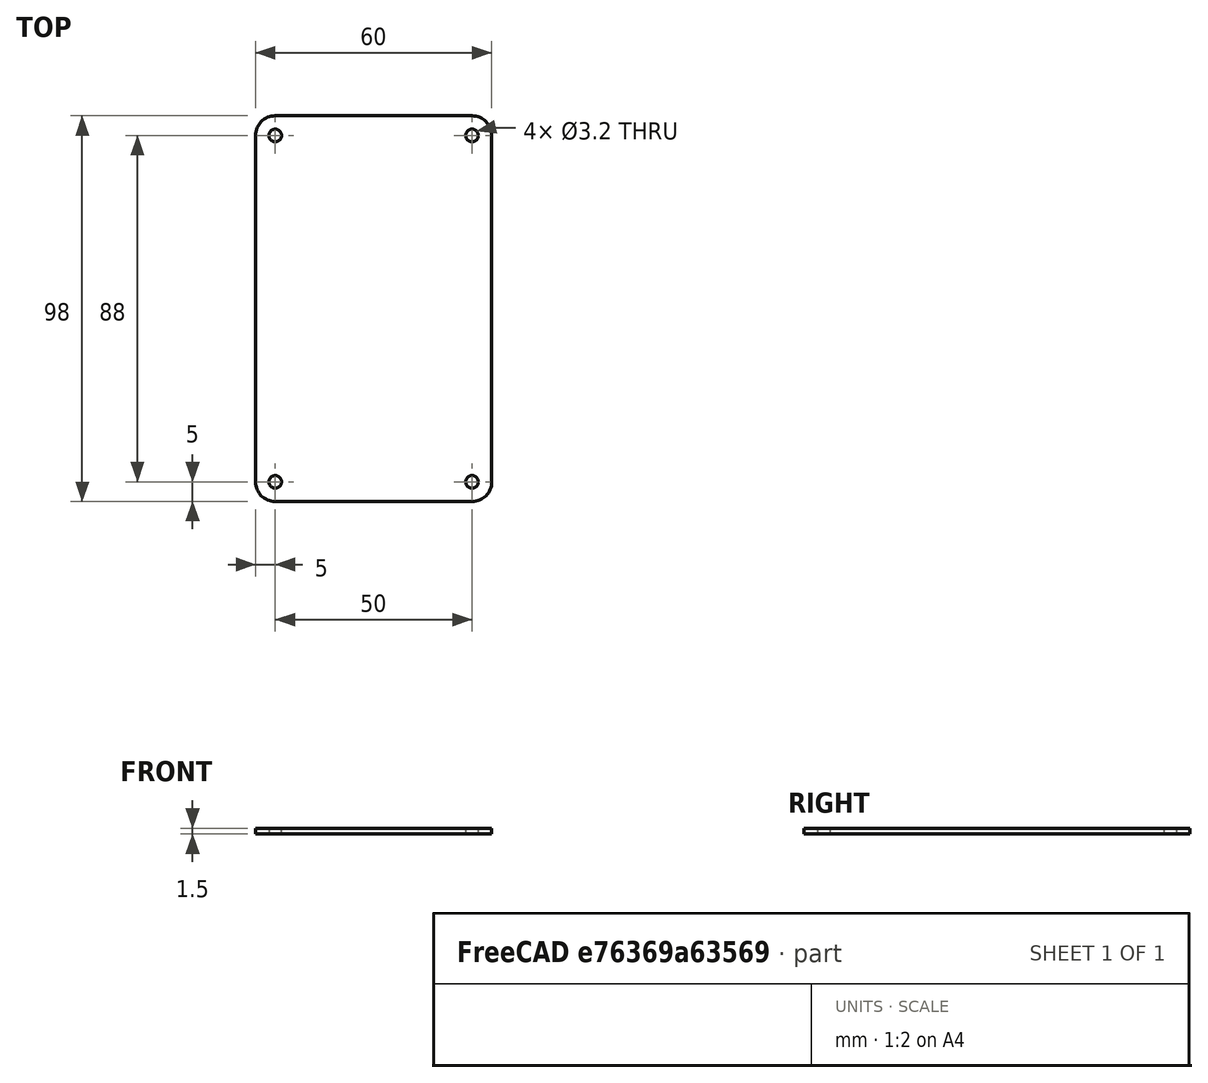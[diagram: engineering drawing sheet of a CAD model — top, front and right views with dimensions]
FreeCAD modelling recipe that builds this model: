
FCSTD DOCUMENT  (FreeCAD 0.17R12802 (Git))
Label: Keep_OUT
License: All rights reserved
LicenseURL: http://en.wikipedia.org/wiki/All_rights_reserved
objects: Sketcher::SketchObject×2, Part::FeaturePython×1, App::DocumentObjectGroupPython×1
note: 3 computed .brp shape members not serialized (recipe doc carries the construction recipe); baked Part::Feature solids carry a one-line shape summary decoded from their .brp

FEATURE [Sketcher::SketchObject] Sketch
  sketch-geometry (8):
    g0: LineSegment StartX=25 StartY=49 StartZ=0 EndX=-25 EndY=49 EndZ=0
    g1: LineSegment StartX=-30 StartY=44 StartZ=0 EndX=-30 EndY=-44 EndZ=0
    g2: LineSegment StartX=-25 StartY=-49 StartZ=0 EndX=25 EndY=-49 EndZ=0
    g3: LineSegment StartX=30 StartY=-44 StartZ=0 EndX=30 EndY=44 EndZ=0
    g4: ArcOfCircle CenterX=-25 CenterY=44 CenterZ=0 NormalX=0 NormalY=0 NormalZ=1 AngleXU=0 Radius=5 StartAngle=1.5708 EndAngle=3.14159
    g5: ArcOfCircle CenterX=-25 CenterY=-44 CenterZ=0 NormalX=0 NormalY=0 NormalZ=1 AngleXU=0 Radius=5 StartAngle=3.14159 EndAngle=4.71239
    g6: ArcOfCircle CenterX=25 CenterY=-44 CenterZ=0 NormalX=0 NormalY=0 NormalZ=1 AngleXU=0 Radius=5 StartAngle=4.71239 EndAngle=6.28319
    g7: ArcOfCircle CenterX=25 CenterY=44 CenterZ=0 NormalX=0 NormalY=0 NormalZ=1 AngleXU=0 Radius=5 StartAngle=0 EndAngle=1.5708
  constraints (20):
    c: Horizontal(g0)
    c: Tangent(g0,g4) = -1.5708
    c: Tangent(g1,g4) = -1.5708
    c: Tangent(g1,g5) = -1.5708
    c: Tangent(g2,g5) = -1.5708
    c: Tangent(g3,g6) = -1.5708
    c: Tangent(g2,g6) = -1.5708
    c: Tangent(g0,g7) = -1.5708
    c: Tangent(g3,g7) = -1.5708
    c: Vertical(g3)
    c: Vertical(g1)
    c: Horizontal(g2)
    c: Radius(g4) = 5
    c: Radius(g7) = 5
    c: DistanceX(g1,g3) = 60
    c: Radius(g5) = 5
    c: Radius(g6) = 5
    c: DistanceY(g2,g0) = 98
    c: DistanceY(g2,g-1) = 49
    c: DistanceX(g-1,g3) = 30
FEATURE [Sketcher::SketchObject] Sketch001
  sketch-geometry (8):
    g0: Circle CenterX=-25 CenterY=44 CenterZ=0 NormalX=0 NormalY=0 NormalZ=1 AngleXU=0 Radius=1.6
    g1: Circle CenterX=25 CenterY=44 CenterZ=0 NormalX=0 NormalY=0 NormalZ=1 AngleXU=0 Radius=1.6
    g2: LineSegment [constr] StartX=-25 StartY=-44 StartZ=0 EndX=25 EndY=-44 EndZ=0
    g3: LineSegment [constr] StartX=25 StartY=-44 StartZ=0 EndX=25 EndY=44 EndZ=0
    g4: LineSegment [constr] StartX=25 StartY=44 StartZ=0 EndX=-25 EndY=44 EndZ=0
    g5: LineSegment [constr] StartX=-25 StartY=44 StartZ=0 EndX=-25 EndY=-44 EndZ=0
    g6: Circle CenterX=-25 CenterY=-44 CenterZ=0 NormalX=0 NormalY=0 NormalZ=1 AngleXU=0 Radius=1.6
    g7: Circle CenterX=25 CenterY=-44 CenterZ=0 NormalX=0 NormalY=0 NormalZ=1 AngleXU=0 Radius=1.6
  constraints (20):
    c: Radius(g0) = 1.6
    c: DistanceX(g0,g-1) = 25
    c: DistanceY(g-1,g0) = 44
    c: Radius(g1) = 1.6
    c: Coincident(g2,g3)
    c: Coincident(g3,g4)
    c: Coincident(g4,g5)
    c: Coincident(g5,g2)
    c: Horizontal(g2)
    c: Horizontal(g4)
    c: Vertical(g3)
    c: Vertical(g5)
    c: Coincident(g3,g1)
    c: Coincident(g4,g0)
    c: DistanceX(g4,g4) = 50
    c: Coincident(g6,g2)
    c: Coincident(g7,g2)
    c: Radius(g7) = 1.6
    c: Radius(g6) = 1.6
    c: DistanceY(g3,g3) = 88
FEATURE [Part::FeaturePython] Board  # WARN: FeaturePython — macro-defined, semantics opaque (R4)
  AutoUpdate = true
  Border = -> Sketch
  Display = true
  Holes = -> Sketch001
  Thickness = 1.5
FEATURE [App::DocumentObjectGroupPython] PCB  # scripted group (container) (typed FeaturePython)
  Group = -> [Board]
